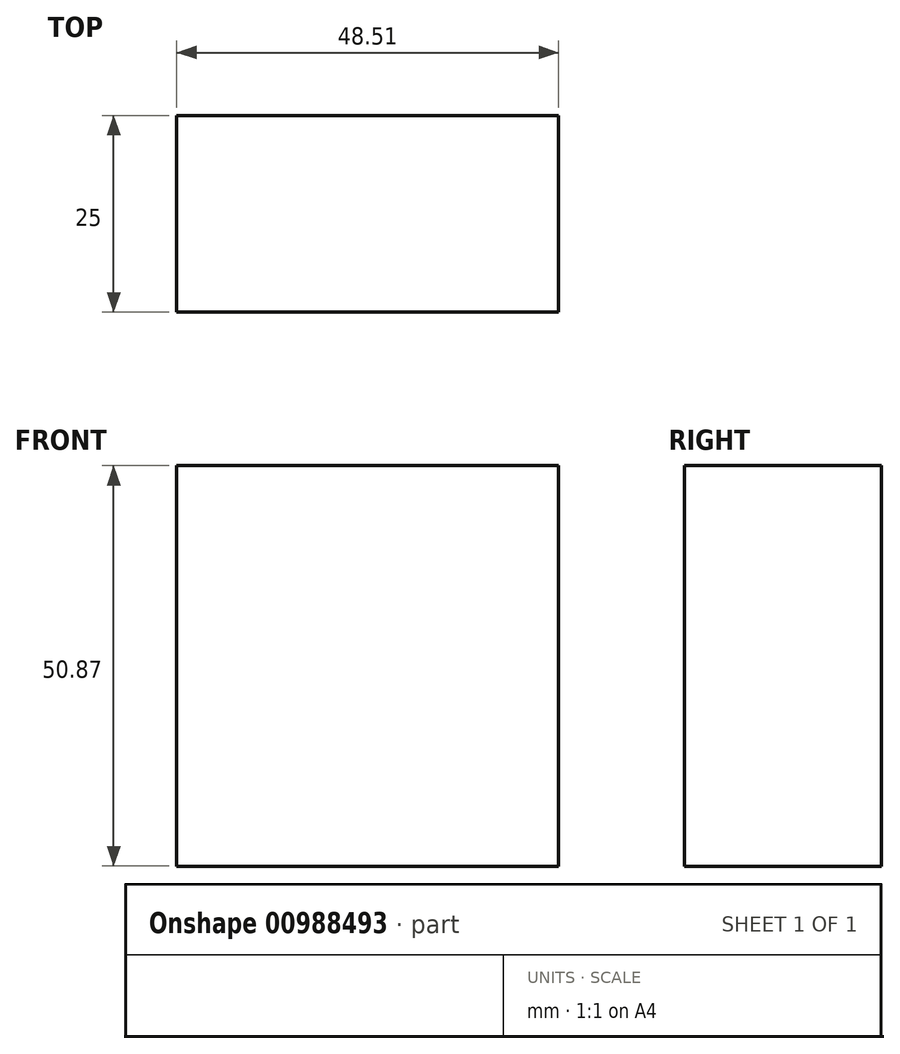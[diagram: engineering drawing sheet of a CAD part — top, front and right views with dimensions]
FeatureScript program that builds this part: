
annotation { "Feature Type Name" : "Feature", "Feature Type Description" : "" }
export const myFeature = defineFeature(function(context is Context, id is Id, definition is map)
    precondition{}
    {
        {
            var Q0;
            Q0=qCreatedBy(makeId("Front.planeOp"),FACE);
            var sketch = newSketch(context, id + "F0", { "sketchPlane" : qUnion([Q0])});
            skLineSegment(sketch, "E0.bottom", {"start": v(-79.34, 35.69) * mm, "end": v(-30.83, 35.69) * mm});
            skLineSegment(sketch, "E0.top", {"start": v(-79.34, -15.18) * mm, "end": v(-30.83, -15.18) * mm});
            skLineSegment(sketch, "E0.left", {"start": v(-79.34, 35.69) * mm, "end": v(-79.34, -15.18) * mm});
            skLineSegment(sketch, "E0.right", {"start": v(-30.83, 35.69) * mm, "end": v(-30.83, -15.18) * mm});
            skSolve(sketch);
        }
        {
            var Q0;
            Q0 = qSketchRegion(id + "F0", true);
            extrude(context, id + "F1", {"entities" : qUnion([Q0]), "depth" : 25 * mm, "offsetDistance" : 25 * mm});
        }
    });
